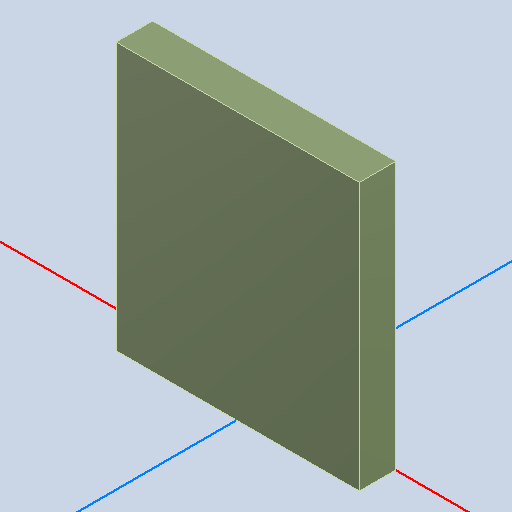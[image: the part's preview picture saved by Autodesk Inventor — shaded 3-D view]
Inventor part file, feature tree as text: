
AUTODESK INVENTOR PART (.ipt)
format: ipt  version: 2022 (Build 260153000, 153)  size: 93,696 bytes
history: native  units: mm
features: other x2, extrude x1
ambient origin geometry x8: Origin, YZ Plane, XZ Plane, XY Plane, X Axis, Y Axis, Z Axis, Center Point
bodies: Body1 (feature_tree)
feature tree (3):
  other  "Твердое тело1"
  extrude  "Выдавливание1"  Depth=1.0mm TaperAngle=0.0deg
  other  "SOT223, U1_SOT223_12"
